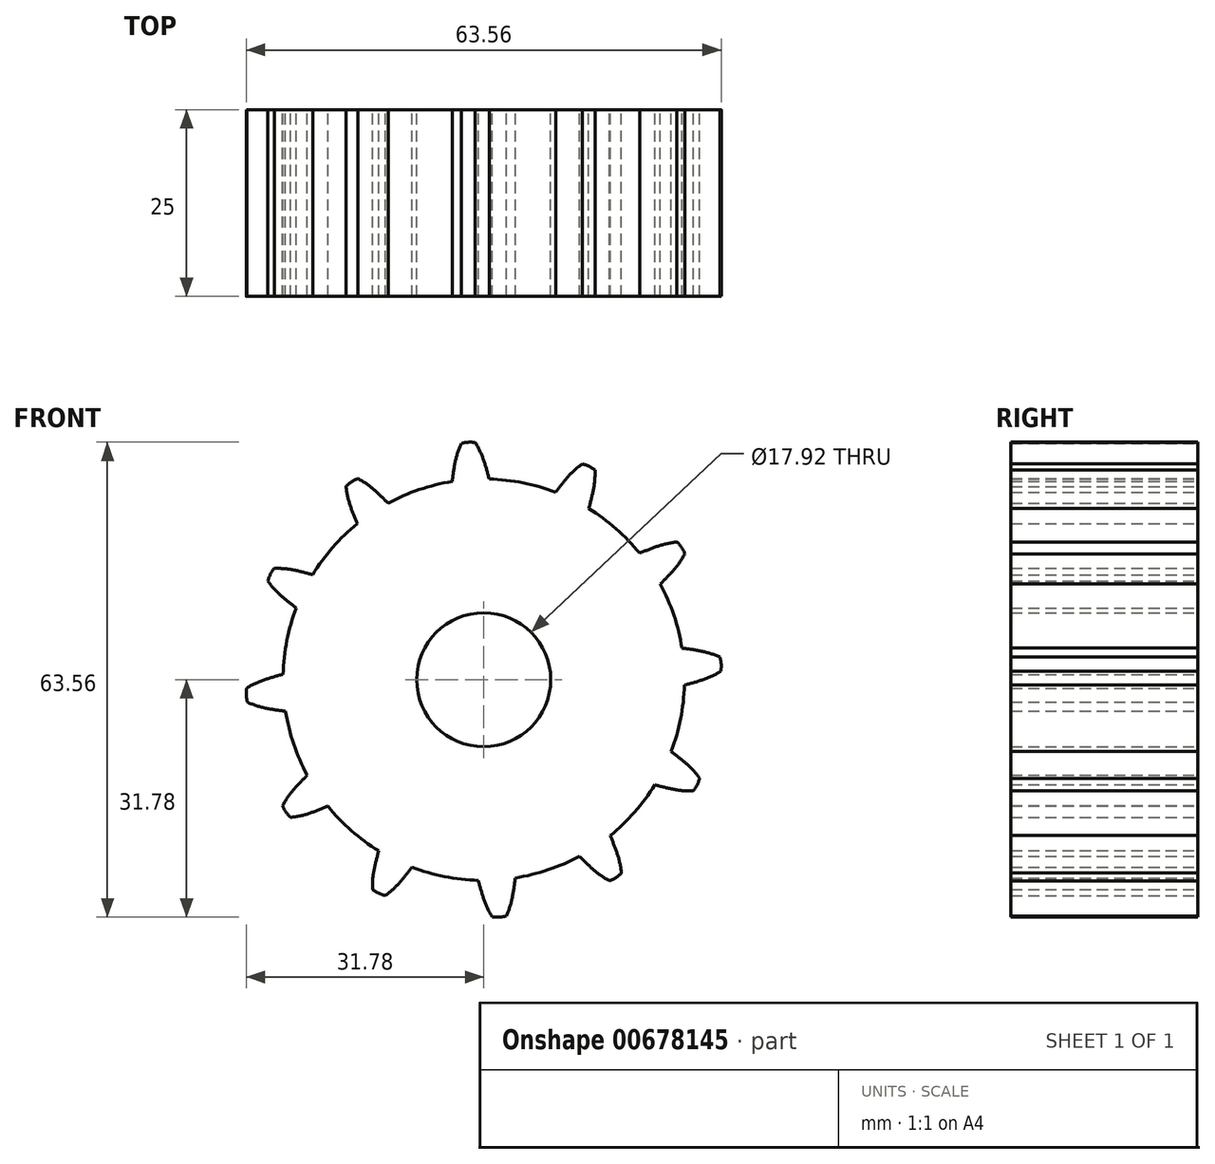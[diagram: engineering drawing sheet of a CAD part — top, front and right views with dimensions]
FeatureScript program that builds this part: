
annotation { "Feature Type Name" : "Feature", "Feature Type Description" : "" }
export const myFeature = defineFeature(function(context is Context, id is Id, definition is map)
    precondition{}
    {
        {
            var Q0;
            Q0=qCreatedBy(makeId("Front.planeOp"),FACE);
            var sketch = newSketch(context, id + "F0", { "sketchPlane" : qUnion([Q0])});
            skCircle(sketch, "E0", {"center": v(0, 0) * mm, "radius": 26.86 * mm});
            skCircle(sketch, "E1", {"center": v(0, 0) * mm, "radius": 29.34 * mm, "construction": true});
            skCircle(sketch, "E2", {"center": v(0, 0) * mm, "radius": 31.75 * mm, "construction": true});
            skLineSegment(sketch, "E3", {"start": v(0, 0) * mm, "end": v(0, 69.47) * mm, "construction": true});
            skLineSegment(sketch, "E4", {"start": v(0, 0) * mm, "end": v(-3.42, 52.18) * mm, "construction": true});
            skLineSegment(sketch, "E5", {"start": v(0, 29.34) * mm, "end": v(-60.52, 29.34) * mm, "construction": true});
            skLineSegment(sketch, "E6", {"start": v(0, 29.34) * mm, "end": v(-63.37, 10.54) * mm, "construction": true});
            skCircle(sketch, "E7", {"center": v(0, 0) * mm, "radius": 28.13 * mm, "construction": true});
            skCircle(sketch, "E8", {"center": v(0, 29.34) * mm, "radius": 16.52 * mm, "construction": true});
            skCircle(sketch, "E9", {"center": v(-15.46, 23.5) * mm, "radius": 16.52 * mm, "construction": true});
            skArc(sketch, "E10", {"start": v(0, 29.34) * mm, "mid": v(-0.5, 30.57) * mm, "end": v(-1.13, 31.73) * mm});
            skArc(sketch, "E11", {"start": v(0.72, 26.85) * mm, "mid": v(0.39, 28.1) * mm, "end": v(0, 29.34) * mm});
            skArc(sketch, "E12.MirrorCS", {"start": v(-3.83, 29.09) * mm, "mid": v(-3.5, 30.37) * mm, "end": v(-3.02, 31.6) * mm});
            skArc(sketch, "E13.MirrorCS", {"start": v(-4.22, 26.53) * mm, "mid": v(-4.05, 27.81) * mm, "end": v(-3.83, 29.09) * mm});
            skArc(sketch, "E14", {"start": v(-1.13, 31.73) * mm, "mid": v(-2.08, 31.77) * mm, "end": v(-3.02, 31.6) * mm});
            skCircle(sketch, "E15", {"center": v(0, 0) * mm, "radius": 8.96 * mm});
            skSolve(sketch);
        }
        {
            var Q0;
            {var subQ0=sQuery(id+"F0.wireOp",EDGE,"E0");var subQ1=makeQuery(id+"F0.imprint","INTERSECT",VERTEX,{"derivedFrom":[subQ0,sQuery(id+"F0.wireOp",EDGE,"E11")]});Q0=makeQuery(id+"F0.imprint","IMPRINT",FACE,{"disambiguationData":[TD([[makeQuery(id+"F0.imprint","IMPRINT",EDGE,{"disambiguationData":[TD([[subQ1,-1.0]])],"derivedFrom":subQ0}),1.0]])]});}
            var Q1;
            Q1=makeQuery(id+"F0.imprint","IMPRINT",FACE,{"disambiguationData":[TD([[makeQuery(id+"F0.imprint","IMPRINT",EDGE,{"derivedFrom":sQuery(id+"F0.wireOp",EDGE,"E10")}),1.0]])]});
            extrude(context, id + "F1", {"entities" : qUnion([Q0, Q1]), "depth" : 25 * mm, "offsetDistance" : 25 * mm});
        }
        {
            var Q0;
            Q0=makeQuery(id+"F1.opExtrude","SWEPT_BODY",BODY,{"disambiguationData":[OSD([sQuery(id+"F0.wireOp",EDGE,"E0"),sQuery(id+"F0.wireOp",EDGE,"E10"),sQuery(id+"F0.wireOp",EDGE,"E11"),sQuery(id+"F0.wireOp",EDGE,"E12.MirrorCS"),sQuery(id+"F0.wireOp",EDGE,"E13.MirrorCS"),sQuery(id+"F0.wireOp",EDGE,"E14")])]});
            var Q1;
            Q1=makeQuery(id+"F1.opExtrude","SWEPT_FACE",FACE,{"disambiguationData":[OSD([sQuery(id+"F0.wireOp",EDGE,"E0")])]});
            circularPattern(context, id + "F2", {"operationType" : NewBodyOperationType.ADD, "entities" : qUnion([Q0]), "axis" : qUnion([Q1]), "angle" : 360 * degree, "instanceCount" : 12, "equalSpace" : true});
        }
    });
